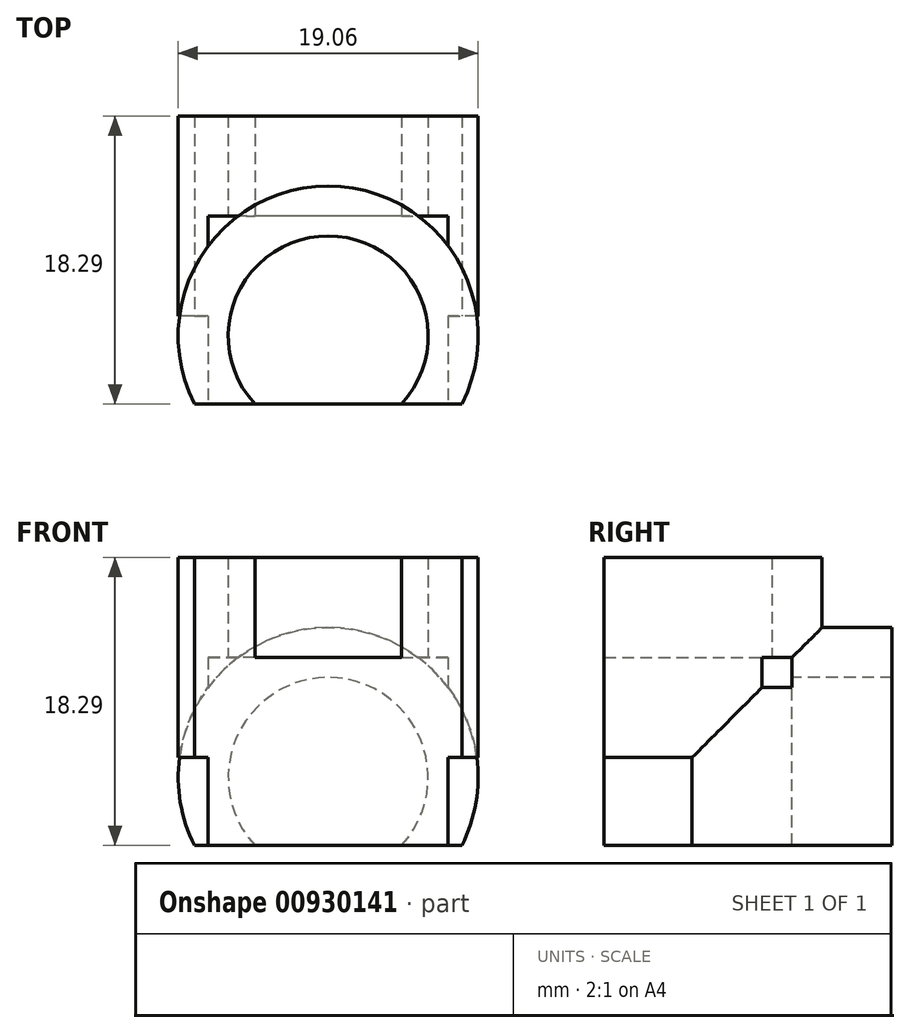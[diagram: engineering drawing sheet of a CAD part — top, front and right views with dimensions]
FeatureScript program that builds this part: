
annotation { "Feature Type Name" : "Feature", "Feature Type Description" : "" }
export const myFeature = defineFeature(function(context is Context, id is Id, definition is map)
    precondition{}
    {
        {
            var Q0;
            Q0=qCreatedBy(makeId("Front.planeOp"),FACE);
            var sketch = newSketch(context, id + "F0", { "sketchPlane" : qUnion([Q0])});
            skLineSegment(sketch, "E0.bottom", {"start": v(7.62, 7.62) * mm, "end": v(-7.62, 7.62) * mm});
            skLineSegment(sketch, "E0.top", {"start": v(7.62, -7.62) * mm, "end": v(-7.62, -7.62) * mm});
            skLineSegment(sketch, "E0.left", {"start": v(7.62, 7.62) * mm, "end": v(7.62, -7.62) * mm});
            skLineSegment(sketch, "E0.right", {"start": v(-7.62, 7.62) * mm, "end": v(-7.62, -7.62) * mm});
            skPoint(sketch, "E0.middle", {"position": v(0, 0) * mm});
            skSolve(sketch);
        }
        {
            var Q0;
            Q0=makeQuery(id+"F0.imprint","IMPRINT",FACE,{"disambiguationData":[TD([[makeQuery(id+"F0.imprint","IMPRINT",EDGE,{"derivedFrom":sQuery(id+"F0.wireOp",EDGE,"E0.bottom")}),1.0]])]});
            extrude(context, id + "F1", {"entities" : qUnion([Q0]), "depth" : 15.24 * mm, "offsetDistance" : 25.4 * mm});
        }
        {
            var Q0;
            Q0=makeQuery(id+"F1.opExtrude","SWEPT_FACE",FACE,{"disambiguationData":[OSD([sQuery(id+"F0.wireOp",EDGE,"E0.bottom")])]});
            var sketch = newSketch(context, id + "F2", { "sketchPlane" : qUnion([Q0])});
            skCircle(sketch, "E1", {"center": v(0, -7.62) * mm, "radius": 6.35 * mm});
            skPoint(sketch, "E1.centerSnap0", {"position": v(7.62, -7.62) * mm});
            skPoint(sketch, "E1.centerSnap1", {"position": v(0, 0) * mm});
            skCircle(sketch, "E2.0", {"center": v(0, -7.62) * mm, "radius": 9.53 * mm});
            skSolve(sketch);
        }
        {
            var Q0;
            Q0 = qSketchRegion(id + "F2", true);
            extrude(context, id + "F3", {"entities" : qUnion([Q0]), "operationType" : NewBodyOperationType.ADD, "depth" : 12.7 * mm, "offsetDistance" : 25.4 * mm, "symmetric" : true});
        }
        {
            var Q0;
            Q0=makeQuery(id+"F1.opExtrude","CAP_FACE",FACE,{"disambiguationData":[OSD([sQuery(id+"F0.wireOp",EDGE,"E0.bottom"),sQuery(id+"F0.wireOp",EDGE,"E0.top"),sQuery(id+"F0.wireOp",EDGE,"E0.left"),sQuery(id+"F0.wireOp",EDGE,"E0.right")])],"isStart":true});
            var sketch = newSketch(context, id + "F4", { "sketchPlane" : qUnion([Q0])});
            skCircle(sketch, "E3", {"center": v(0, 0) * mm, "radius": 6.35 * mm});
            skCircle(sketch, "E4.0", {"center": v(0, 0) * mm, "radius": 9.53 * mm});
            skSolve(sketch);
        }
        {
            var Q0;
            Q0 = qSketchRegion(id + "F4", true);
            extrude(context, id + "F5", {"entities" : qUnion([Q0]), "operationType" : NewBodyOperationType.ADD, "depth" : 12.7 * mm, "offsetDistance" : 25.4 * mm, "symmetric" : true});
        }
        {
            var Q0;
            Q0=makeQuery(id+"F1.opExtrude","SWEPT_FACE",FACE,{"disambiguationData":[OSD([sQuery(id+"F0.wireOp",EDGE,"E0.bottom")])]});
            var sketch = newSketch(context, id + "F6", { "sketchPlane" : qUnion([Q0])});
            skCircle(sketch, "E5", {"center": v(0, -7.62) * mm, "radius": 6.35 * mm});
            skSolve(sketch);
        }
        {
            var Q0;
            Q0 = qSketchRegion(id + "F6", true);
            extrude(context, id + "F7", {"entities" : qUnion([Q0]), "operationType" : NewBodyOperationType.REMOVE, "depth" : 25.4 * mm, "offsetDistance" : 25.4 * mm});
        }
        {
            var Q0;
            Q0=makeQuery(id+"F1.opExtrude","CAP_FACE",FACE,{"disambiguationData":[OSD([sQuery(id+"F0.wireOp",EDGE,"E0.bottom"),sQuery(id+"F0.wireOp",EDGE,"E0.top"),sQuery(id+"F0.wireOp",EDGE,"E0.left"),sQuery(id+"F0.wireOp",EDGE,"E0.right")])],"isStart":true});
            var sketch = newSketch(context, id + "F8", { "sketchPlane" : qUnion([Q0])});
            skCircle(sketch, "E6", {"center": v(0, 0) * mm, "radius": 6.35 * mm});
            skSolve(sketch);
        }
        {
            var Q0;
            Q0 = qSketchRegion(id + "F8", true);
            extrude(context, id + "F9", {"entities" : qUnion([Q0]), "operationType" : NewBodyOperationType.REMOVE, "depth" : 25.4 * mm, "offsetDistance" : 25.4 * mm});
        }
        {
            var Q0;
            Q0=qCreatedBy(makeId("Right.planeOp"),FACE);
            var sketch = newSketch(context, id + "F10", { "sketchPlane" : qUnion([Q0])});
            skLineSegment(sketch, "E7", {"start": v(13.44, -4.32) * mm, "end": v(-11.94, -4.32) * mm});
            skLineSegment(sketch, "E8", {"start": v(-11.94, -4.32) * mm, "end": v(-11.94, 21.06) * mm});
            skLineSegment(sketch, "E9", {"start": v(-11.94, 21.06) * mm, "end": v(-22.52, 21.06) * mm});
            skLineSegment(sketch, "E10", {"start": v(-22.52, 21.06) * mm, "end": v(-22.52, -14.9) * mm});
            skLineSegment(sketch, "E11", {"start": v(-22.52, -14.9) * mm, "end": v(13.44, -14.9) * mm});
            skLineSegment(sketch, "E12", {"start": v(13.44, -14.9) * mm, "end": v(13.44, -4.32) * mm});
            skSolve(sketch);
        }
        {
            var Q0;
            Q0 = qSketchRegion(id + "F10", true);
            extrude(context, id + "F11", {"entities" : qUnion([Q0]), "operationType" : NewBodyOperationType.REMOVE, "oppositeDirection" : true, "depth" : 25.4 * mm, "offsetDistance" : 25.4 * mm, "symmetric" : true});
        }
    });
